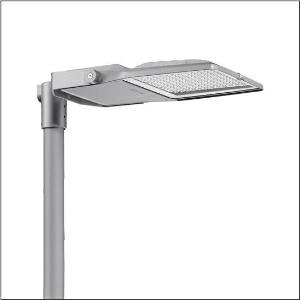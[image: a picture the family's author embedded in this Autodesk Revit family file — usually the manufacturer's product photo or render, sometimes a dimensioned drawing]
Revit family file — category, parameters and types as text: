
# Revit family: floodlight_fl_21_iq_midi___pl33t_5xa7782e4f3a_344b
name_source: partatom
category: Lighting Fixtures
units: mm (PartAtom-declared; Revit-internal decimal feet)

## family parameters
Cut with Voids When Loaded = No
Host = Face
Light Source = No
Part Type = Normal
Room Calculation Point = No
Round Connector Dimension = Use Diameter
Shared = No

## types (1)
- --- (1 x LED, 27690 lm, 208.1 W, 4000K)
    Apparent Load = 208 VA
    CIE Flux Codes = 26 75 99 100 100
    Color Rendering = 70
    Color Temperature = 4000K
    Default Elevation = 1800 mm
    Description = Floodlight FL 21 iQ midi, floodlight, primary light control with lens, of PMMA, primary optical cover: protective disc, of toughened safety glass, transparent, light distribution: PL33T, light emission: direct distribution, installation type: surface-mounted, LED, High Power LED, rated luminous flux: 27.690lm, luminous efficacy: 133lm/W, light colour: 740, colour temperature: 4000K, control gear: ECG iQ, control: optimised constant luminous flux control (CLO 2.0), Desk-Remote (wireless, voltage-free reading and setting of iQ features in the workshop via application-optimized NFC function/RFID function), Smart-Wire, Night-Set, Temp-Guard, Auto-Match, Street-Remote, with terminal, 6-pole, mains connection: 220..240V, AC, 50/60Hz, start of lifetime: 208W, end of service life: 227W, reduction: 90W, luminaire housing, of diecast aluminium, powder-coated, Siteco® metallic grey (DB 702S), corrosivity category C5 mid according to DIN EN ISO 12944, sealing non-destructively replaceable, please order mast flange separately, mast bracket, of steel, galvanised, powder-coated, Siteco® metallic grey (DB 702S), protection rating (complete): IP66, insulation class (complete): insulation class II (safety insulation), certification: CE, protection symbol: D, impact resistance: IK08, permissible operating ambient temperature: -40..+40°C, permissible operating ambient temperature for outdoor applications: -40..+50°C, standard: DIN EN 12944, LABS conformity tested according to VDMA 24364:2018-05, packaging unit: 1 piece

Light Distribution: PL33T
    Height = 76 mm
    Lamp = 1 x LED
    Lamp Light Flux = 27690 lm
    Lamp Power = 208.1 W
    Lamp count = 1
    Length = 657 mm
    Luminous efficacy = 133 lm/W
    Manufacturer = Siteco
    ModVariant = No
    Model = 5XA7782E4F3A
    Number of Poles = 1
    OnlyDefault = Yes
    Power Factor = 1
    Product Name = Floodlight FL 21 iQ midi | PL33T
    Product group = floodlight | pylon annexe
    ProductGroupID = 6200
    Protection Class = Protection class II
    Protection Degree = IP 66
    RLX_Detail_Level = 1
    RLX_Emergency_Light_Flux = 0 lm
    RLX_Emergency_Type = 0
    RLX_Emergency_Type_DB = No
    RlxData = <blob elided: 153369 chars, md5=1fb2daf6>
    Socket = socket
    Standby Power = 0 W
    System Light Flux = 27690 lm
    System Power = 208 W
    Type Comments = factory setting: luminous flux: 100 % | dim-lin: 254 | 710 mA
    Type Image = l_1007123.jpg
    URL = http://relux.com
    VarID = @adj_033843
    Voltage = 0 V
    Weight = 0.00 kg
    Width = 442 mm

## geometry (parser evidence)
native form markers: Blend x4, Sweep x13
no freeform markers — native parametric forms only
